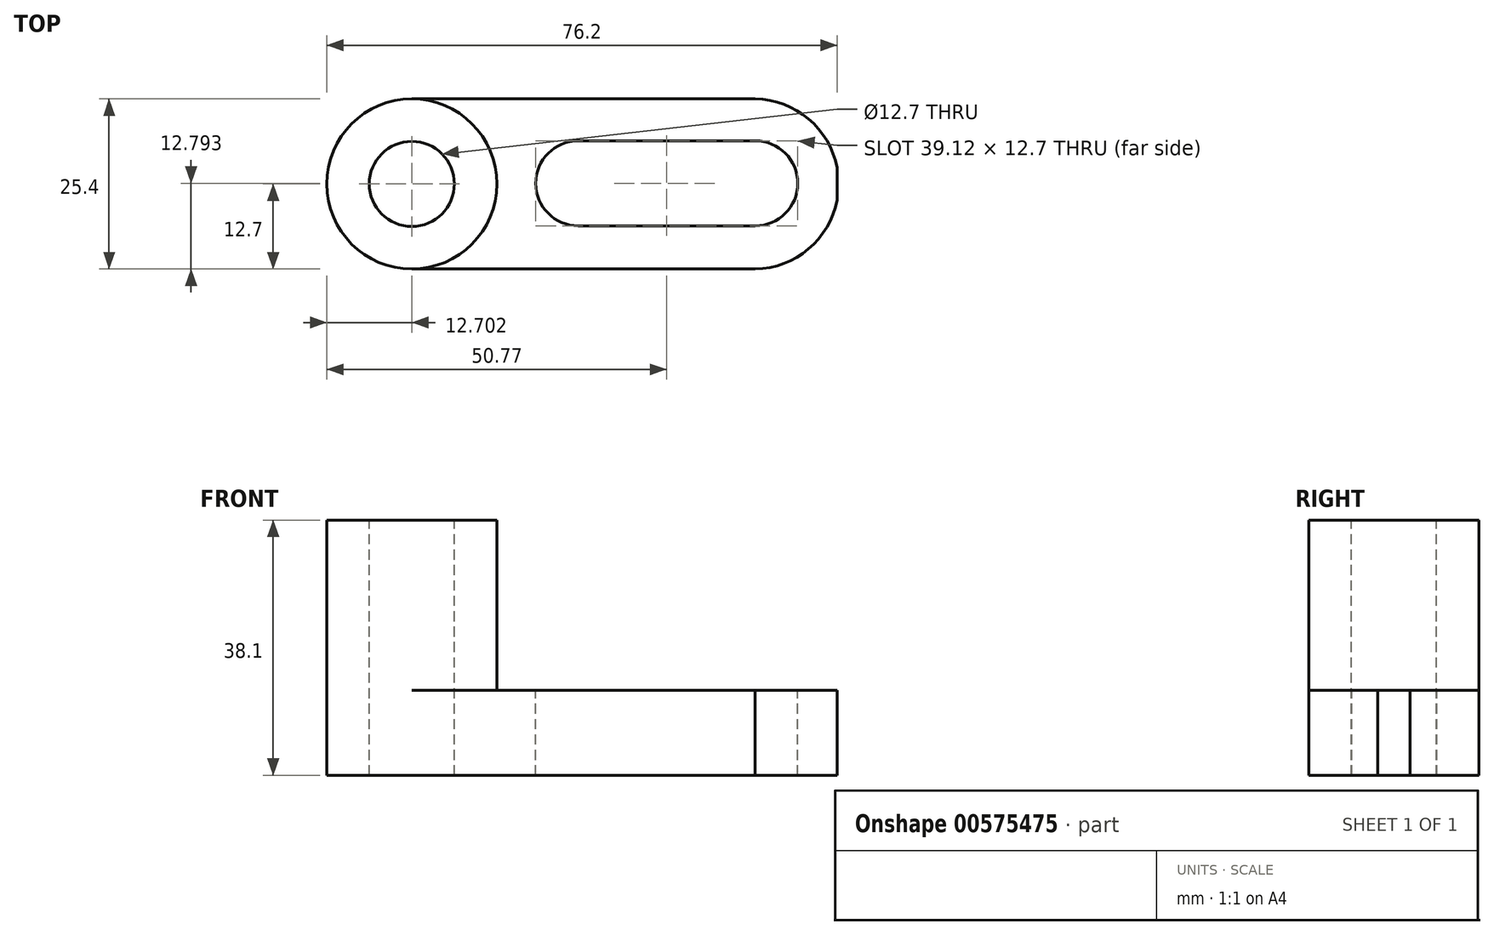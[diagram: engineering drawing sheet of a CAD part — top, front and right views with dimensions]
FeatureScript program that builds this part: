
annotation { "Feature Type Name" : "Feature", "Feature Type Description" : "" }
export const myFeature = defineFeature(function(context is Context, id is Id, definition is map)
    precondition{}
    {
        {
            var Q0;
            Q0=qCreatedBy(makeId("Front.planeOp"),FACE);
            var sketch = newSketch(context, id + "F0", { "sketchPlane" : qUnion([Q0])});
            skLineSegment(sketch, "E0", {"start": v(-80.34, 38.1) * mm, "end": v(-80.34, 0) * mm});
            skLineSegment(sketch, "E1", {"start": v(-80.34, 0) * mm, "end": v(-4.14, 0) * mm});
            skLineSegment(sketch, "E2", {"start": v(-4.14, 0) * mm, "end": v(-4.14, 12.7) * mm});
            skLineSegment(sketch, "E3", {"start": v(-4.14, 12.7) * mm, "end": v(-54.94, 12.7) * mm});
            skLineSegment(sketch, "E4", {"start": v(-54.94, 12.7) * mm, "end": v(-54.94, 38.1) * mm});
            skLineSegment(sketch, "E5", {"start": v(-54.94, 38.1) * mm, "end": v(-80.34, 38.1) * mm});
            skSolve(sketch);
        }
        {
            var Q0;
            Q0=makeQuery(id+"F0.imprint","IMPRINT",FACE,{"disambiguationData":[TD([[makeQuery(id+"F0.imprint","IMPRINT",EDGE,{"derivedFrom":sQuery(id+"F0.wireOp",EDGE,"E0")}),1.0]])]});
            extrude(context, id + "F1", {"entities" : qUnion([Q0]), "depth" : 25.4 * mm, "offsetDistance" : 25.4 * mm});
        }
        {
            var Q0;
            Q0=makeQuery(id+"F1.opExtrude","SWEPT_FACE",FACE,{"disambiguationData":[OSD([sQuery(id+"F0.wireOp",EDGE,"E3")])]});
            var sketch = newSketch(context, id + "F2", { "sketchPlane" : qUnion([Q0])});
            skCircle(sketch, "E6", {"center": v(-16.36, -12.6) * mm, "radius": 6.35 * mm});
            skCircle(sketch, "E7", {"center": v(-42.78, -12.6) * mm, "radius": 6.35 * mm});
            skLineSegment(sketch, "E8", {"start": v(-42.78, -6.26) * mm, "end": v(-16.36, -6.26) * mm});
            skLineSegment(sketch, "E9", {"start": v(-42.78, -18.96) * mm, "end": v(-16.36, -18.96) * mm});
            skArc(sketch, "E10", {"start": v(-16.36, -25.4) * mm, "mid": v(-3.9, -12.7) * mm, "end": v(-16.36, 0) * mm});
            skSolve(sketch);
        }
        {
            var Q0;
            {var subQ0=sQuery(id+"F2.wireOp",EDGE,"E7");var subQ1=makeQuery(id+"F2.imprint","INTERSECT",VERTEX,{"derivedFrom":[subQ0,sQuery(id+"F2.wireOp",EDGE,"E8")]});Q0=makeQuery(id+"F2.imprint","IMPRINT",FACE,{"disambiguationData":[TD([[makeQuery(id+"F2.imprint","IMPRINT",EDGE,{"disambiguationData":[TD([[subQ1,-1.0]])],"derivedFrom":subQ0}),1.0]])]});}
            var Q1;
            {var subQ0=sQuery(id+"F2.wireOp",EDGE,"E8");Q1=makeQuery(id+"F2.imprint","IMPRINT",FACE,{"disambiguationData":[TD([[makeQuery(id+"F2.imprint","IMPRINT",EDGE,{"derivedFrom":subQ0}),-1.0]])]});}
            var Q2;
            {var subQ0=sQuery(id+"F2.wireOp",EDGE,"E6");var subQ1=makeQuery(id+"F2.imprint","INTERSECT",VERTEX,{"derivedFrom":[subQ0,sQuery(id+"F2.wireOp",EDGE,"E8")]});Q2=makeQuery(id+"F2.imprint","IMPRINT",FACE,{"disambiguationData":[TD([[makeQuery(id+"F2.imprint","IMPRINT",EDGE,{"disambiguationData":[TD([[subQ1,-1.0]])],"derivedFrom":subQ0}),1.0]])]});}
            var Q3;
            {var subQ0=sQuery(id+"F2.wireOp",EDGE,"E10");var subQ1=sQuery(id+"F0.wireOp",EDGE,"E3");var subQ2=makeQuery(id+"F1.opExtrude","CAP_EDGE",EDGE,{"disambiguationData":[OSD([subQ1])],"isStart":true});var subQ3=makeQuery(id+"F2.imprint","INTERSECT",VERTEX,{"derivedFrom":[subQ2,subQ0]});Q3=makeQuery(id+"F2.imprint","IMPRINT",FACE,{"disambiguationData":[TD([[makeQuery(id+"F2.imprint","IMPRINT",EDGE,{"disambiguationData":[TD([[subQ3,1.0]])],"derivedFrom":subQ0}),-1.0]])]});}
            var Q4;
            {var subQ0=sQuery(id+"F2.wireOp",EDGE,"E10");var subQ1=sQuery(id+"F0.wireOp",EDGE,"E3");var subQ2=makeQuery(id+"F1.opExtrude","CAP_EDGE",EDGE,{"disambiguationData":[OSD([subQ1])],"isStart":false});var subQ3=makeQuery(id+"F2.imprint","INTERSECT",VERTEX,{"derivedFrom":[subQ2,subQ0]});Q4=makeQuery(id+"F2.imprint","IMPRINT",FACE,{"disambiguationData":[TD([[makeQuery(id+"F2.imprint","IMPRINT",EDGE,{"disambiguationData":[TD([[subQ3,-1.0]])],"derivedFrom":subQ0}),-1.0]])]});}
            extrude(context, id + "F3", {"entities" : qUnion([Q0, Q1, Q2, Q3, Q4]), "operationType" : NewBodyOperationType.REMOVE, "endBound" : BoundingType.THROUGH_ALL, "oppositeDirection" : true, "depth" : 25.4 * mm, "offsetDistance" : 25.4 * mm});
        }
        {
            var Q0;
            Q0=makeQuery(id+"F1.opExtrude","SWEPT_FACE",FACE,{"disambiguationData":[OSD([sQuery(id+"F0.wireOp",EDGE,"E5")])]});
            var sketch = newSketch(context, id + "F4", { "sketchPlane" : qUnion([Q0])});
            skCircle(sketch, "E11", {"center": v(-67.64, -12.7) * mm, "radius": 12.7 * mm});
            skPoint(sketch, "E11.centerSnap0", {"position": v(-67.64, 0) * mm});
            skPoint(sketch, "E11.centerSnap1", {"position": v(-54.94, -12.7) * mm});
            skCircle(sketch, "E12", {"center": v(-67.64, -12.7) * mm, "radius": 6.35 * mm});
            skSolve(sketch);
        }
        {
            var Q0;
            {var subQ0=sQuery(id+"F4.wireOp",EDGE,"E11");var subQ1=sQuery(id+"F0.wireOp",EDGE,"E5");var subQ2=makeQuery(id+"F1.opExtrude","CAP_EDGE",EDGE,{"disambiguationData":[OSD([subQ1])],"isStart":true});var subQ3=makeQuery(id+"F4.imprint","INTERSECT",VERTEX,{"derivedFrom":[subQ2,subQ0]});Q0=makeQuery(id+"F4.imprint","IMPRINT",FACE,{"disambiguationData":[TD([[makeQuery(id+"F4.imprint","IMPRINT",EDGE,{"disambiguationData":[TD([[subQ3,-1.0]])],"derivedFrom":subQ0}),-1.0]])]});}
            var Q1;
            {var subQ0=sQuery(id+"F4.wireOp",EDGE,"E11");var subQ1=sQuery(id+"F0.wireOp",EDGE,"E5");var subQ4=makeQuery(id+"F1.opExtrude","CAP_EDGE",EDGE,{"disambiguationData":[OSD([subQ1])],"isStart":false});var subQ5=makeQuery(id+"F4.imprint","INTERSECT",VERTEX,{"derivedFrom":[subQ4,subQ0]});Q1=makeQuery(id+"F4.imprint","IMPRINT",FACE,{"disambiguationData":[TD([[makeQuery(id+"F4.imprint","IMPRINT",EDGE,{"disambiguationData":[TD([[subQ5,1.0]])],"derivedFrom":subQ0}),-1.0]])]});}
            var Q2;
            Q2=makeQuery(id+"F4.imprint","IMPRINT",FACE,{"disambiguationData":[TD([[makeQuery(id+"F4.imprint","IMPRINT",EDGE,{"derivedFrom":sQuery(id+"F4.wireOp",EDGE,"E12")}),1.0]])]});
            extrude(context, id + "F5", {"entities" : qUnion([Q0, Q1, Q2]), "operationType" : NewBodyOperationType.REMOVE, "endBound" : BoundingType.THROUGH_ALL, "oppositeDirection" : true, "depth" : 25.4 * mm, "offsetDistance" : 25.4 * mm});
        }
        {
            var Q0;
            Q0=makeQuery(id+"F1.opExtrude","SWEPT_FACE",FACE,{"disambiguationData":[OSD([sQuery(id+"F0.wireOp",EDGE,"E5")])]});
            var sketch = newSketch(context, id + "F6", { "sketchPlane" : qUnion([Q0])});
            skArc(sketch, "E13", {"start": v(-67.64, -25.4) * mm, "mid": v(-54.94, -12.7) * mm, "end": v(-67.64, 0) * mm});
            skSolve(sketch);
        }
        {
            var Q0;
            {var subQ1=sQuery(id+"F0.wireOp",EDGE,"E5");var subQ2=makeQuery(id+"F1.opExtrude","CAP_EDGE",EDGE,{"disambiguationData":[OSD([subQ1])],"isStart":true});var subQ3=subQ2;Q0=makeQuery(id+"F6.imprint","IMPRINT",FACE,{"disambiguationData":[TD([[makeQuery(id+"F6.imprint","IMPRINT",EDGE,{"derivedFrom":subQ3}),1.0]])]});}
            var Q1;
            {var subQ1=sQuery(id+"F0.wireOp",EDGE,"E5");var subQ2=makeQuery(id+"F1.opExtrude","CAP_EDGE",EDGE,{"disambiguationData":[OSD([subQ1])],"isStart":false});var subQ3=subQ2;Q1=makeQuery(id+"F6.imprint","IMPRINT",FACE,{"disambiguationData":[TD([[makeQuery(id+"F6.imprint","IMPRINT",EDGE,{"derivedFrom":subQ3}),-1.0]])]});}
            extrude(context, id + "F7", {"entities" : qUnion([Q0, Q1]), "operationType" : NewBodyOperationType.REMOVE, "oppositeDirection" : true, "depth" : 25.4 * mm, "offsetDistance" : 25.4 * mm});
        }
    });
